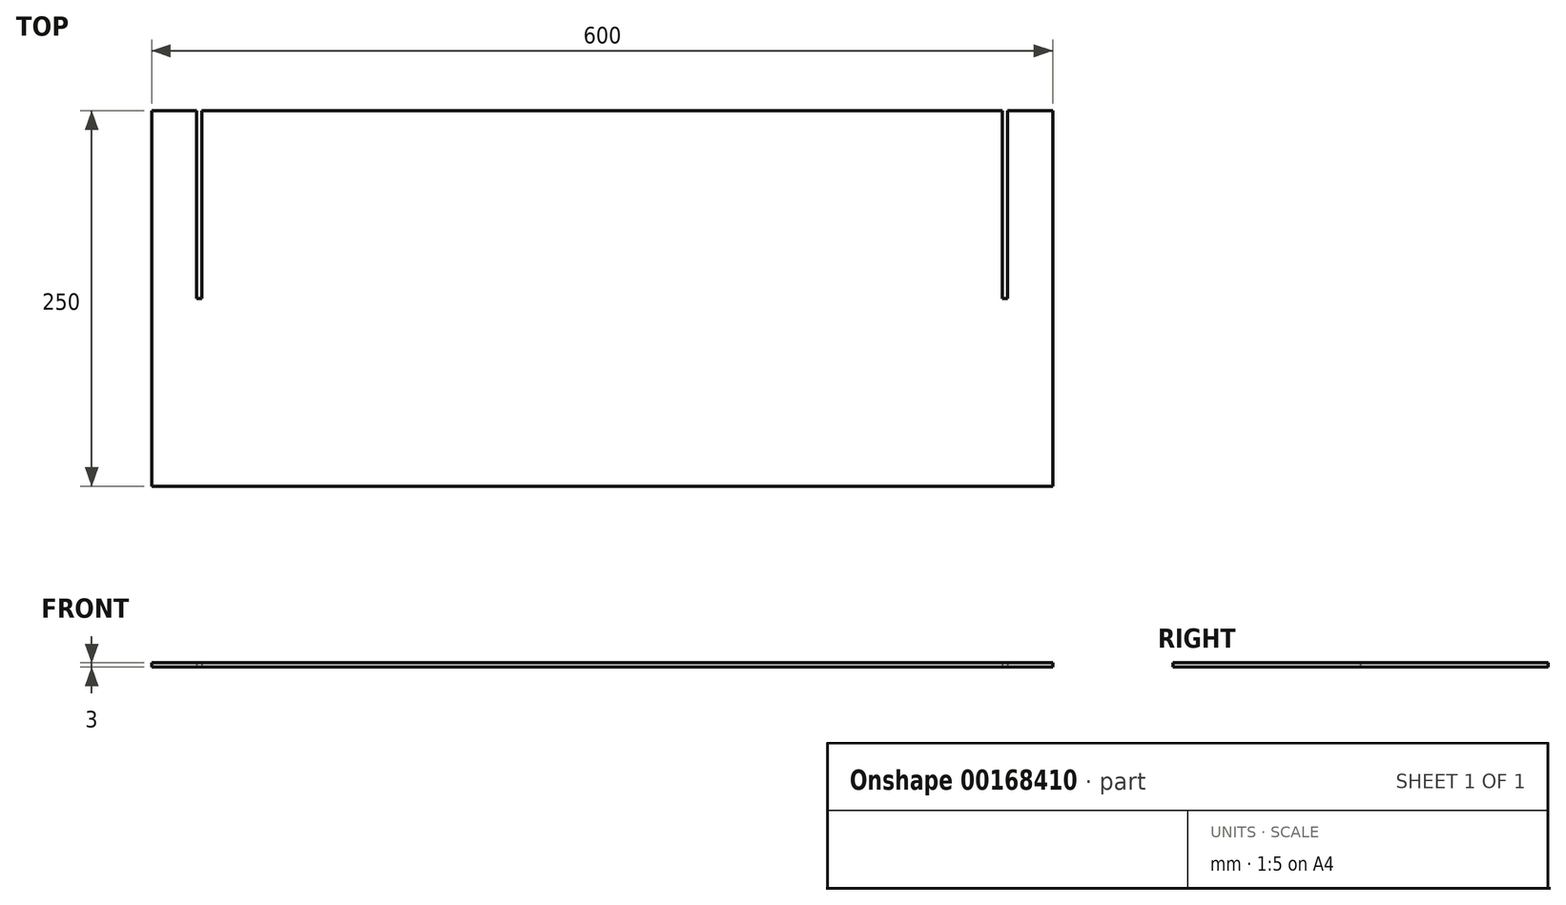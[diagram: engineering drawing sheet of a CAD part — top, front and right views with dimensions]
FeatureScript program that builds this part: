
annotation { "Feature Type Name" : "Feature", "Feature Type Description" : "" }
export const myFeature = defineFeature(function(context is Context, id is Id, definition is map)
    precondition{}
    {
        {
            var Q0;
            Q0=qCreatedBy(makeId("Top.planeOp"),FACE);
            var sketch = newSketch(context, id + "F0", { "sketchPlane" : qUnion([Q0])});
            skLineSegment(sketch, "E0.bottom", {"start": v(292.05, -72.38) * mm, "end": v(262.05, -72.38) * mm});
            skLineSegment(sketch, "E0.top", {"start": v(292.05, -322.38) * mm, "end": v(-307.95, -322.38) * mm});
            skLineSegment(sketch, "E0.left", {"start": v(292.05, -72.38) * mm, "end": v(292.05, -322.38) * mm});
            skLineSegment(sketch, "E0.right", {"start": v(-307.95, -72.38) * mm, "end": v(-307.95, -322.38) * mm});
            skPoint(sketch, "E1.oppositeSnap0", {"position": v(-307.95, -197.38) * mm});
            skLineSegment(sketch, "E1.top", {"start": v(-277.95, -197.38) * mm, "end": v(-274.45, -197.38) * mm});
            skLineSegment(sketch, "E1.left", {"start": v(-277.95, -72.38) * mm, "end": v(-277.95, -197.38) * mm});
            skLineSegment(sketch, "E1.right", {"start": v(-274.45, -72.38) * mm, "end": v(-274.45, -197.38) * mm});
            skLineSegment(sketch, "E2.trimOffspring", {"start": v(-277.95, -72.38) * mm, "end": v(-307.95, -72.38) * mm});
            skLineSegment(sketch, "E3", {"start": v(-7.95, -322.38) * mm, "end": v(-7.95, -72.38) * mm, "construction": true});
            skLineSegment(sketch, "E4.MirrorCS", {"start": v(262.05, -72.38) * mm, "end": v(262.05, -197.38) * mm});
            skLineSegment(sketch, "E5.MirrorCS", {"start": v(258.55, -72.38) * mm, "end": v(258.55, -197.38) * mm});
            skLineSegment(sketch, "E6.MirrorCS", {"start": v(262.05, -197.38) * mm, "end": v(258.55, -197.38) * mm});
            skLineSegment(sketch, "E7.trimOffspring", {"start": v(258.55, -72.38) * mm, "end": v(-274.45, -72.38) * mm});
            skSolve(sketch);
        }
        {
            var Q0;
            Q0=makeQuery(id+"F0.imprint","IMPRINT",FACE,{"disambiguationData":[TD([[makeQuery(id+"F0.imprint","IMPRINT",EDGE,{"derivedFrom":sQuery(id+"F0.wireOp",EDGE,"E0.bottom")}),1.0]])]});
            extrude(context, id + "F1", {"entities" : qUnion([Q0]), "depth" : 3 * mm});
        }
    });
